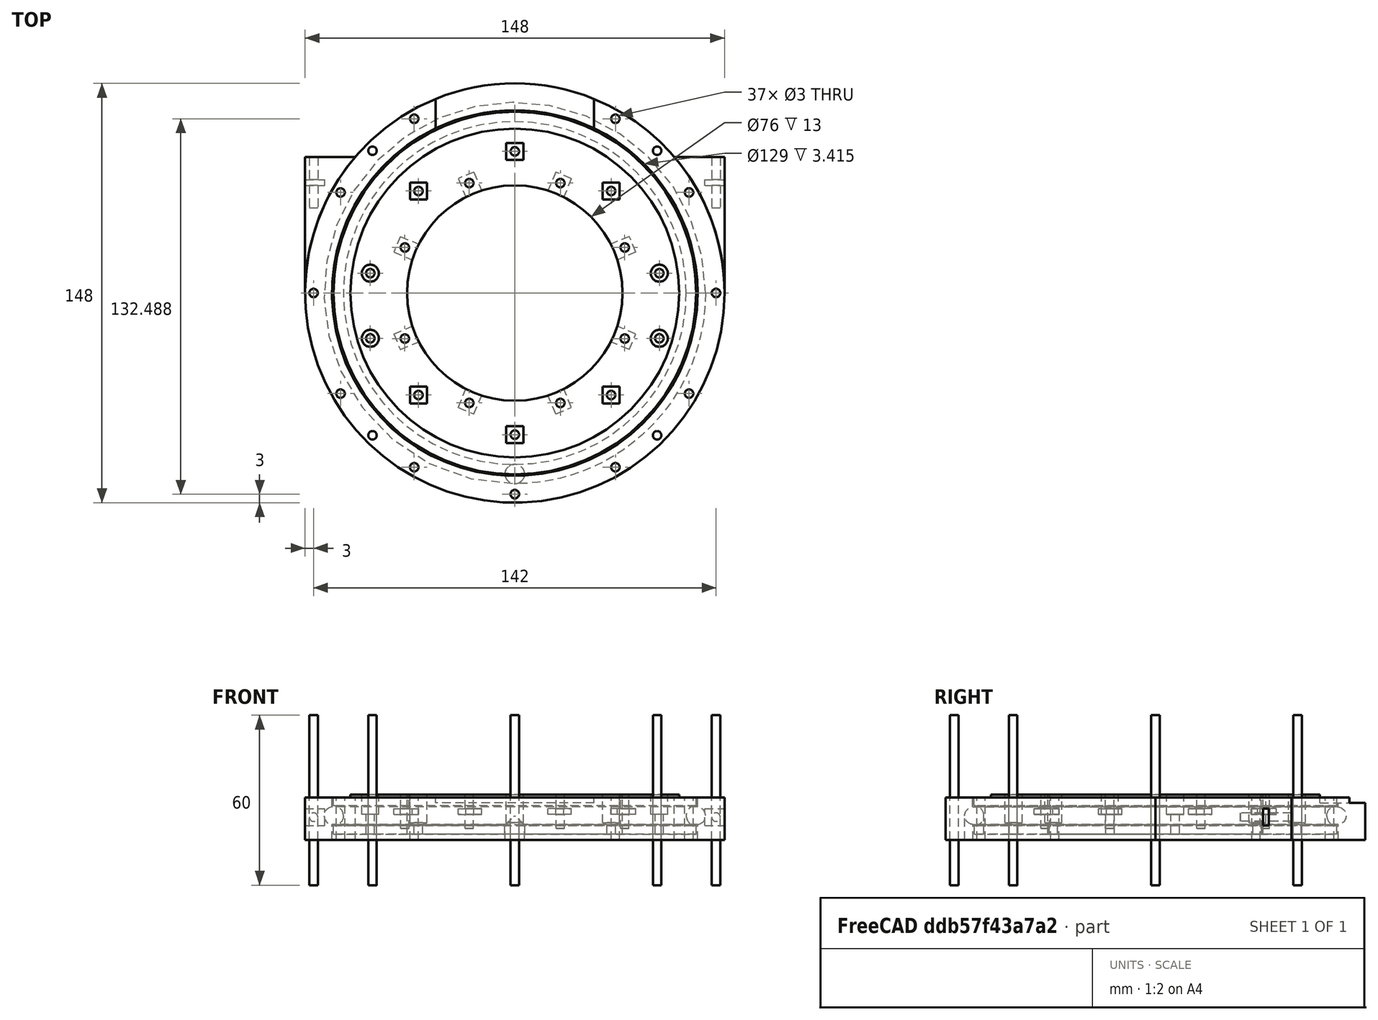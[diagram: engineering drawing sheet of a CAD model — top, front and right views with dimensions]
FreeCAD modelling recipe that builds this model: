
FCSTD DOCUMENT  (FreeCAD 0.19R24291 (Git))
Label: bazovina-part-E_lozo-okruh_011
License: All rights reserved
LicenseURL: http://en.wikipedia.org/wiki/All_rights_reserved
objects: Part::Cylinder×58, Part::Box×24, Part::Cut×18, Part::Compound×14, Part::FeaturePython×3, Part::Torus×2, Mesh::Feature×1
note: 119 computed .brp shape members not serialized (recipe doc carries the construction recipe); baked Part::Feature solids carry a one-line shape summary decoded from their .brp

FEATURE [Part::Torus] Torus001  label="Anuloid001"
  Angle1 = -180
  Angle2 = 180
  Angle3 = 360
  AttacherType = Attacher::AttachEngine3D
  Placement = pos=(0,0,24.5) rot=(0,0,1;0rad)
  Radius1 = 64.2
  Radius2 = 3.1
FEATURE [Part::Cylinder] Cylinder476  label="Válec476"
  Angle = 360
  AttacherType = Attacher::AttachEngine3D
  Height = 20
  Placement = pos=(0,-63.8,4.5) rot=(0,0,1;0rad)
  Radius = 3.5
FEATURE [Part::FeaturePython] Tube024  # WARN: FeaturePython — macro-defined, semantics opaque (R4)
  AttacherType = Attacher::AttachEngine3D
  Height = 15
  InnerRadius = 64.5
  OuterRadius = 74
  Placement = pos=(0,0,16) rot=(0,0,1;0rad)
FEATURE [Part::Cut] Cut
  Base = -> Tube024
  Tool = -> Torus001
FEATURE [Part::Cut] Cut176
  Base = -> Cut
  Tool = -> Cylinder476
FEATURE [Part::Box] Box176  label="Krychle176"
  AttacherType = Attacher::AttachEngine3D
  Height = 15
  Length = 148
  Placement = pos=(-74,0,16) rot=(0,0,1;0rad)
  Width = 48
FEATURE [Part::Cylinder] Cylinder482  label="Válec482"
  Angle = 360
  AttacherType = Attacher::AttachEngine3D
  Height = 15
  Placement = pos=(0,0,16) rot=(0,0,1;0rad)
  Radius = 74
FEATURE [Part::Cut] Cut185
  Base = -> Box176
  Tool = -> Cylinder482
FEATURE [Part::Cylinder] Cylinder485  label="Válec485"
  Angle = 360
  AttacherType = Attacher::AttachEngine3D
  Height = 15
  Placement = pos=(0,0,16) rot=(0,0,1;0rad)
  Radius = 74
FEATURE [Part::Cut] Cut188
  Base = -> Cut185
  Tool = -> Cylinder485
FEATURE [Part::Cylinder] Cylinder510  label="Válec510"
  Angle = 360
  AttacherType = Attacher::AttachEngine3D
  Height = 50
  Placement = pos=(-71,80,24) rot=(1,0,0;1.5708rad)
  Radius = 1.5
FEATURE [Part::Cylinder] Cylinder511  label="Válec511"
  Angle = 360
  AttacherType = Attacher::AttachEngine3D
  Height = 60
  Placement = pos=(0,-71,0) rot=(0,0,1;0rad)
  Radius = 1.5
FEATURE [Part::Cylinder] Cylinder513  label="Válec513"
  Angle = 360
  AttacherType = Attacher::AttachEngine3D
  Height = 60
  Placement = pos=(-50.2046,-50.2046,0) rot=(0,0,-1;0.785398rad)
  Radius = 1.5
FEATURE [Part::Cylinder] Cylinder518  label="Válec518"
  Angle = 360
  AttacherType = Attacher::AttachEngine3D
  Height = 60
  Placement = pos=(71,5e-15,0) rot=(0,0,1;1.5708rad)
  Radius = 1.5
FEATURE [Part::Box] Box209  label="Krychle209"
  AttacherType = Attacher::AttachEngine3D
  Height = 6
  Length = 8
  Placement = pos=(-75,38,21) rot=(0,0,1;0rad)
  Width = 2
FEATURE [Part::Box] Box208  label="Krychle208"
  AttacherType = Attacher::AttachEngine3D
  Height = 6
  Length = 8
  Placement = pos=(67,38,21) rot=(0,0,1;0rad)
  Width = 2
FEATURE [Part::Cylinder] Cylinder517  label="Válec517"
  Angle = 360
  AttacherType = Attacher::AttachEngine3D
  Height = 60
  Placement = pos=(50.2046,50.2046,0) rot=(0,0,1;2.35619rad)
  Radius = 1.5
FEATURE [Part::Cylinder] Cylinder509  label="Válec509"
  Angle = 360
  AttacherType = Attacher::AttachEngine3D
  Height = 50
  Placement = pos=(71,80,24) rot=(1,0,0;1.5708rad)
  Radius = 1.5
FEATURE [Part::Cylinder] Cylinder514  label="Válec514"
  Angle = 360
  AttacherType = Attacher::AttachEngine3D
  Height = 60
  Placement = pos=(-50.2046,50.2046,0) rot=(0,0,1;3.92699rad)
  Radius = 1.5
FEATURE [Part::Cylinder] Cylinder516  label="Válec516"
  Angle = 360
  AttacherType = Attacher::AttachEngine3D
  Height = 60
  Placement = pos=(50.2046,-50.2046,0) rot=(0,0,1;0.785398rad)
  Radius = 1.5
FEATURE [Part::Cylinder] Cylinder512  label="Válec512"
  Angle = 360
  AttacherType = Attacher::AttachEngine3D
  Height = 60
  Placement = pos=(-71,-2.8e-14,0) rot=(0,0,-1;1.5708rad)
  Radius = 1.5
FEATURE [Part::Compound] Compound340
  Links = -> [Cylinder511,Cylinder516,Cylinder518,Cylinder517,Cylinder514,Cylinder512,Cylinder513]
FEATURE [Part::Compound] Compound339
  Links = -> [Cylinder509,Cylinder510]
FEATURE [Part::Compound] Compound338
  Links = -> [Box208,Box209]
FEATURE [Part::Compound] Compound337
  Links = -> [Cut188,Cut176]
FEATURE [Part::Cut] Cut201
  Base = -> Compound337
  Tool = -> Compound338
FEATURE [Part::Cut] Cut202
  Base = -> Cut201
  Tool = -> Compound339
FEATURE [Part::Box] Box179  label="Krychle179"
  AttacherType = Attacher::AttachEngine3D
  Height = 47
  Length = 56
  Placement = pos=(-28,0,29) rot=(0,0,1;0rad)
  Width = 200
FEATURE [Part::Cylinder] Cylinder288  label="Válec288"
  Angle = 360
  AttacherType = Attacher::AttachEngine3D
  Height = 20
  Placement = pos=(0,-64,4.5) rot=(0,0,1;0rad)
  Radius = 3.5
FEATURE [Part::Cylinder] Cylinder372  label="Válec372"
  Angle = 360
  AttacherType = Attacher::AttachEngine3D
  Height = 50
  Placement = pos=(-34,-36,0) rot=(0,0,1;0rad)
  Radius = 1.5
FEATURE [Part::Cylinder] Cylinder371  label="Válec371"
  Angle = 360
  AttacherType = Attacher::AttachEngine3D
  Height = 50
  Placement = pos=(34,36,0) rot=(0,0,1;0rad)
  Radius = 1.5
FEATURE [Part::Torus] Torus  label="Anuloid"
  Angle1 = -180
  Angle2 = 180
  Angle3 = 360
  AttacherType = Attacher::AttachEngine3D
  Placement = pos=(0,0,24.5) rot=(0,0,1;0rad)
  Radius1 = 64
  Radius2 = 3.5
FEATURE [Part::FeaturePython] Tube019  # WARN: FeaturePython — macro-defined, semantics opaque (R4)
  AttacherType = Attacher::AttachEngine3D
  Height = 13
  InnerRadius = 38
  OuterRadius = 64
  Placement = pos=(0,0,18) rot=(0,0,1;0rad)
FEATURE [Part::FeaturePython] Tube020  # WARN: FeaturePython — macro-defined, semantics opaque (R4)
  AttacherType = Attacher::AttachEngine3D
  Height = 1
  InnerRadius = 38
  OuterRadius = 58
  Placement = pos=(0,0,31) rot=(0,0,1;0rad)
FEATURE [Part::Cut] Cut129
  Base = -> Tube019
  Tool = -> Torus
FEATURE [Part::Cut] Cut130
  Base = -> Cut129
  Tool = -> Cylinder288
FEATURE [Part::Cylinder] Cylinder370  label="Válec370"
  Angle = 360
  AttacherType = Attacher::AttachEngine3D
  Height = 50
  Placement = pos=(-34,36,0) rot=(0,0,1;0rad)
  Radius = 1.5
FEATURE [Part::Cylinder] Cylinder374  label="Válec374"
  Angle = 360
  AttacherType = Attacher::AttachEngine3D
  Height = 50
  Placement = pos=(0,50,0) rot=(0,0,1;0rad)
  Radius = 1.5
FEATURE [Part::Cylinder] Cylinder377  label="Válec377"
  Angle = 360
  AttacherType = Attacher::AttachEngine3D
  Height = 50
  Placement = pos=(51,7,0) rot=(0,0,1;0rad)
  Radius = 1.5
FEATURE [Part::Cylinder] Cylinder409  label="Válec409"
  Angle = 360
  AttacherType = Attacher::AttachEngine3D
  Height = 7
  Placement = pos=(51,7,50) rot=(0,0,1;0rad)
  Radius = 3
FEATURE [Part::Cylinder] Cylinder376  label="Válec376"
  Angle = 360
  AttacherType = Attacher::AttachEngine3D
  Height = 100
  Placement = pos=(-51,-16,0) rot=(0,0,1;0rad)
  Radius = 1.5
FEATURE [Part::Cylinder] Cylinder375  label="Válec375"
  Angle = 360
  AttacherType = Attacher::AttachEngine3D
  Height = 50
  Placement = pos=(0,-50,0) rot=(0,0,1;0rad)
  Radius = 1.5
FEATURE [Part::Cylinder] Cylinder404  label="Válec404"
  Angle = 360
  AttacherType = Attacher::AttachEngine3D
  Height = 7
  Placement = pos=(-51,7,50) rot=(0,0,1;0rad)
  Radius = 3
FEATURE [Part::Cylinder] Cylinder373  label="Válec373"
  Angle = 360
  AttacherType = Attacher::AttachEngine3D
  Height = 50
  Placement = pos=(34,-36,0) rot=(0,0,1;0rad)
  Radius = 1.5
FEATURE [Part::Cylinder] Cylinder408  label="Válec408"
  Angle = 360
  AttacherType = Attacher::AttachEngine3D
  Height = 7
  Placement = pos=(-51,-16,50) rot=(0,0,1;0rad)
  Radius = 3
FEATURE [Part::Box] Box149  label="Krychle149"
  AttacherType = Attacher::AttachEngine3D
  Height = 10
  Length = 6
  Placement = pos=(-37,33,40) rot=(0,0,1;0rad)
  Width = 6
FEATURE [Part::Box] Box150  label="Krychle150"
  AttacherType = Attacher::AttachEngine3D
  Height = 10
  Length = 6
  Placement = pos=(31,-39,40) rot=(0,0,1;0rad)
  Width = 6
FEATURE [Part::Cylinder] Cylinder378  label="Válec378"
  Angle = 360
  AttacherType = Attacher::AttachEngine3D
  Height = 50
  Placement = pos=(-51,7,0) rot=(0,0,1;0rad)
  Radius = 1.5
FEATURE [Part::Cylinder] Cylinder379  label="Válec379"
  Angle = 360
  AttacherType = Attacher::AttachEngine3D
  Height = 100
  Placement = pos=(51,-16,0) rot=(0,0,1;0rad)
  Radius = 1.5
FEATURE [Part::Compound] Compound308
  Links = -> [Cylinder370,Cylinder371,Cylinder372,Cylinder373,Cylinder374,Cylinder375,Cylinder376,Cylinder377,Cylinder378,Cylinder379]
FEATURE [Part::Cut] Cut160
  Base = -> Cut130
  Tool = -> Compound308
FEATURE [Part::Cylinder] Cylinder411  label="Válec411"
  Angle = 360
  AttacherType = Attacher::AttachEngine3D
  Height = 7
  Placement = pos=(51,-16,50) rot=(0,0,1;0rad)
  Radius = 3
FEATURE [Part::Cylinder] Cylinder406  label="Válec406"
  Angle = 360
  AttacherType = Attacher::AttachEngine3D
  Height = 7
  Placement = pos=(-51,-16,50) rot=(0,0,1;0rad)
  Radius = 3
FEATURE [Part::Cylinder] Cylinder405  label="Válec405"
  Angle = 360
  AttacherType = Attacher::AttachEngine3D
  Height = 7
  Placement = pos=(51,7,50) rot=(0,0,1;0rad)
  Radius = 3
FEATURE [Part::Box] Box153  label="Krychle153"
  AttacherType = Attacher::AttachEngine3D
  Height = 10
  Length = 6
  Placement = pos=(-37,33,40) rot=(0,0,1;0rad)
  Width = 6
FEATURE [Part::Cylinder] Cylinder410  label="Válec410"
  Angle = 360
  AttacherType = Attacher::AttachEngine3D
  Height = 7
  Placement = pos=(-51,7,50) rot=(0,0,1;0rad)
  Radius = 3
FEATURE [Part::Compound] Compound313
  Links = -> [Cylinder408,Cylinder411,Cylinder409,Cylinder410]
  Placement = pos=(0,0,-25) rot=(0,0,1;0rad)
FEATURE [Part::Cut] Cut162
  Base = -> Cut160
  Tool = -> Compound313
FEATURE [Part::Cylinder] Cylinder407  label="Válec407"
  Angle = 360
  AttacherType = Attacher::AttachEngine3D
  Height = 7
  Placement = pos=(51,-16,50) rot=(0,0,1;0rad)
  Radius = 3
FEATURE [Part::Compound] Compound312
  Links = -> [Cylinder406,Cylinder407,Cylinder405,Cylinder404]
  Placement = pos=(0,0,-25) rot=(0,0,1;0rad)
FEATURE [Part::Cut] Cut161
  Base = -> Tube020
  Tool = -> Compound312
FEATURE [Part::Box] Box148  label="Krychle148"
  AttacherType = Attacher::AttachEngine3D
  Height = 10
  Length = 6
  Placement = pos=(31,33,40) rot=(0,0,1;0rad)
  Width = 6
FEATURE [Part::Box] Box146  label="Krychle146"
  AttacherType = Attacher::AttachEngine3D
  Height = 10
  Length = 6
  Placement = pos=(-3,-53,40) rot=(0,0,1;0rad)
  Width = 6
FEATURE [Part::Box] Box145  label="Krychle145"
  AttacherType = Attacher::AttachEngine3D
  Height = 10
  Length = 6
  Placement = pos=(-3,47,40) rot=(0,0,1;0rad)
  Width = 6
FEATURE [Part::Box] Box147  label="Krychle147"
  AttacherType = Attacher::AttachEngine3D
  Height = 10
  Length = 6
  Placement = pos=(-37,-39,40) rot=(0,0,1;0rad)
  Width = 6
FEATURE [Part::Compound] Compound315
  Links = -> [Box145,Box147,Box146,Box148,Box149,Box150]
  Placement = pos=(0,0,-18) rot=(0,0,1;0rad)
FEATURE [Part::Cut] Cut164
  Base = -> Cut162
  Tool = -> Compound315
FEATURE [Part::Box] Box151  label="Krychle151"
  AttacherType = Attacher::AttachEngine3D
  Height = 10
  Length = 6
  Placement = pos=(-3,-53,40) rot=(0,0,1;0rad)
  Width = 6
FEATURE [Part::Box] Box157  label="Krychle157"
  AttacherType = Attacher::AttachEngine3D
  Height = 2
  Length = 6
  Placement = pos=(14.4491,-42.7226,25) rot=(0,0,1;0.392699rad)
  Width = 8
FEATURE [Part::Box] Box162  label="Krychle162"
  AttacherType = Attacher::AttachEngine3D
  Height = 2
  Length = 6
  Placement = pos=(-40.4265,19.9924,25) rot=(0,0,-1;1.96349rad)
  Width = 8
FEATURE [Part::Box] Box159  label="Krychle159"
  AttacherType = Attacher::AttachEngine3D
  Height = 2
  Length = 6
  Placement = pos=(42.7226,14.4491,25) rot=(0,0,1;1.96349rad)
  Width = 8
FEATURE [Part::Box] Box156  label="Krychle156"
  AttacherType = Attacher::AttachEngine3D
  Height = 10
  Length = 6
  Placement = pos=(31,-39,40) rot=(0,0,1;0rad)
  Width = 6
FEATURE [Part::Box] Box154  label="Krychle154"
  AttacherType = Attacher::AttachEngine3D
  Height = 10
  Length = 6
  Placement = pos=(-37,-39,40) rot=(0,0,1;0rad)
  Width = 6
FEATURE [Part::Box] Box158  label="Krychle158"
  AttacherType = Attacher::AttachEngine3D
  Height = 2
  Length = 6
  Placement = pos=(40.4265,-19.9924,25) rot=(0,0,1;1.1781rad)
  Width = 8
FEATURE [Part::Box] Box152  label="Krychle152"
  AttacherType = Attacher::AttachEngine3D
  Height = 10
  Length = 6
  Placement = pos=(-3,47,40) rot=(0,0,1;0rad)
  Width = 6
FEATURE [Part::Box] Box155  label="Krychle155"
  AttacherType = Attacher::AttachEngine3D
  Height = 10
  Length = 6
  Placement = pos=(31,33,40) rot=(0,0,1;0rad)
  Width = 6
FEATURE [Part::Compound] Compound316
  Links = -> [Box152,Box154,Box151,Box155,Box153,Box156]
  Placement = pos=(0,0,-18) rot=(0,0,1;0rad)
FEATURE [Part::Cut] Cut163
  Base = -> Cut161
  Tool = -> Compound316
FEATURE [Part::Cylinder] Cylinder471  label="Válec471"
  Angle = 360
  AttacherType = Attacher::AttachEngine3D
  Height = 100
  Placement = pos=(16.0727,38.8029,0) rot=(0,0,1;3.14159rad)
  Radius = 1.5
FEATURE [Part::Cylinder] Cylinder474  label="Válec474"
  Angle = 360
  AttacherType = Attacher::AttachEngine3D
  Height = 100
  Placement = pos=(-38.8029,-16.0727,0) rot=(0,0,-1;0.785398rad)
  Radius = 1.5
FEATURE [Part::Box] Box163  label="Krychle163"
  AttacherType = Attacher::AttachEngine3D
  Height = 2
  Length = 6
  Placement = pos=(-42.7226,-14.4491,25) rot=(0,0,-1;1.1781rad)
  Width = 8
FEATURE [Part::Cylinder] Cylinder446  label="Válec446"
  Angle = 360
  AttacherType = Attacher::AttachEngine3D
  Height = 100
  Placement = pos=(38.8029,16.0727,0) rot=(0,0,1;2.35619rad)
  Radius = 1.5
FEATURE [Part::Cylinder] Cylinder448  label="Válec448"
  Angle = 360
  AttacherType = Attacher::AttachEngine3D
  Height = 100
  Placement = pos=(-16.0727,38.8029,0) rot=(0,0,1;3.92699rad)
  Radius = 1.5
FEATURE [Part::Box] Box161  label="Krychle161"
  AttacherType = Attacher::AttachEngine3D
  Height = 2
  Length = 6
  Placement = pos=(-14.4491,42.7226,25) rot=(0,0,1;3.53429rad)
  Width = 8
FEATURE [Part::Cylinder] Cylinder449  label="Válec449"
  Angle = 360
  AttacherType = Attacher::AttachEngine3D
  Height = 100
  Placement = pos=(-38.8029,16.0727,0) rot=(0,0,-1;1.5708rad)
  Radius = 1.5
FEATURE [Part::Cylinder] Cylinder451  label="Válec451"
  Angle = 360
  AttacherType = Attacher::AttachEngine3D
  Height = 100
  Placement = pos=(-16.0727,-38.8029,0) rot=(0,0,1;0rad)
  Radius = 1.5
FEATURE [Part::Cylinder] Cylinder444  label="Válec444"
  Angle = 360
  AttacherType = Attacher::AttachEngine3D
  Height = 100
  Placement = pos=(16.0727,-38.8029,0) rot=(0,0,1;0.785398rad)
  Radius = 1.5
FEATURE [Part::Cylinder] Cylinder473  label="Válec473"
  Angle = 360
  AttacherType = Attacher::AttachEngine3D
  Height = 100
  Placement = pos=(-38.8029,16.0727,0) rot=(0,0,-1;1.5708rad)
  Radius = 1.5
FEATURE [Part::Box] Box164  label="Krychle164"
  AttacherType = Attacher::AttachEngine3D
  Height = 2
  Length = 6
  Placement = pos=(-19.9924,-40.4265,25) rot=(0,0,-1;0.392699rad)
  Width = 8
FEATURE [Part::Box] Box160  label="Krychle160"
  AttacherType = Attacher::AttachEngine3D
  Height = 2
  Length = 6
  Placement = pos=(19.9924,40.4265,25) rot=(0,0,1;2.74889rad)
  Width = 8
FEATURE [Part::Compound] Compound322
  Links = -> [Box157,Box158,Box159,Box160,Box161,Box162,Box163,Box164]
FEATURE [Part::Cylinder] Cylinder445  label="Válec445"
  Angle = 360
  AttacherType = Attacher::AttachEngine3D
  Height = 100
  Placement = pos=(38.8029,-16.0727,0) rot=(0,0,1;1.5708rad)
  Radius = 1.5
FEATURE [Part::Cylinder] Cylinder450  label="Válec450"
  Angle = 360
  AttacherType = Attacher::AttachEngine3D
  Height = 100
  Placement = pos=(-38.8029,-16.0727,0) rot=(0,0,-1;0.785398rad)
  Radius = 1.5
FEATURE [Part::Cylinder] Cylinder447  label="Válec447"
  Angle = 360
  AttacherType = Attacher::AttachEngine3D
  Height = 100
  Placement = pos=(16.0727,38.8029,0) rot=(0,0,1;3.14159rad)
  Radius = 1.5
FEATURE [Part::Compound] Compound325
  Links = -> [Cylinder444,Cylinder445,Cylinder446,Cylinder447,Cylinder448,Cylinder449,Cylinder450,Cylinder451]
FEATURE [Part::Cut] Cut173
  Base = -> Cut163
  Tool = -> Compound325
FEATURE [Part::Cylinder] Cylinder468  label="Válec468"
  Angle = 360
  AttacherType = Attacher::AttachEngine3D
  Height = 100
  Placement = pos=(16.0727,-38.8029,0) rot=(0,0,1;0.785398rad)
  Radius = 1.5
FEATURE [Part::Cylinder] Cylinder469  label="Válec469"
  Angle = 360
  AttacherType = Attacher::AttachEngine3D
  Height = 100
  Placement = pos=(38.8029,-16.0727,0) rot=(0,0,1;1.5708rad)
  Radius = 1.5
FEATURE [Part::Cylinder] Cylinder472  label="Válec472"
  Angle = 360
  AttacherType = Attacher::AttachEngine3D
  Height = 100
  Placement = pos=(-16.0727,38.8029,0) rot=(0,0,1;3.92699rad)
  Radius = 1.5
FEATURE [Part::Cylinder] Cylinder470  label="Válec470"
  Angle = 360
  AttacherType = Attacher::AttachEngine3D
  Height = 100
  Placement = pos=(38.8029,16.0727,0) rot=(0,0,1;2.35619rad)
  Radius = 1.5
FEATURE [Part::Cylinder] Cylinder475  label="Válec475"
  Angle = 360
  AttacherType = Attacher::AttachEngine3D
  Height = 100
  Placement = pos=(-16.0727,-38.8029,0) rot=(0,0,1;0rad)
  Radius = 1.5
FEATURE [Part::Compound] Compound328
  Links = -> [Cylinder468,Cylinder469,Cylinder470,Cylinder471,Cylinder472,Cylinder473,Cylinder474,Cylinder475]
  Placement = pos=(0,0,20) rot=(0,0,1;0rad)
FEATURE [Part::Cut] Cut174
  Base = -> Cut164
  Tool = -> Compound328
FEATURE [Part::Cut] Cut175
  Base = -> Cut174
  Tool = -> Compound322
FEATURE [Part::Compound] Compound336  label="bazovina-part-C"
  Links = -> [Cut173,Cut175]
FEATURE [Part::Cylinder] Cylinder974  label="Válec974"
  Angle = 360
  AttacherType = Attacher::AttachEngine3D
  Height = 60
  Placement = pos=(35.5,-61.4878,0) rot=(0,0,1;0.523599rad)
  Radius = 1.5
FEATURE [Part::Cylinder] Cylinder976  label="Válec976"
  Angle = 360
  AttacherType = Attacher::AttachEngine3D
  Height = 60
  Placement = pos=(71,-1.8e-14,0) rot=(0,0,1;1.5708rad)
  Radius = 1.5
FEATURE [Part::Cylinder] Cylinder973  label="Válec973"
  Angle = 360
  AttacherType = Attacher::AttachEngine3D
  Height = 60
  Placement = pos=(0,-71,0) rot=(0,0,1;0rad)
  Radius = 1.5
FEATURE [Part::Cylinder] Cylinder975  label="Válec975"
  Angle = 360
  AttacherType = Attacher::AttachEngine3D
  Height = 60
  Placement = pos=(61.4878,-35.5,0) rot=(0,0,1;1.0472rad)
  Radius = 1.5
FEATURE [Part::Cylinder] Cylinder978  label="Válec978"
  Angle = 360
  AttacherType = Attacher::AttachEngine3D
  Height = 60
  Placement = pos=(35.5,61.4878,0) rot=(0,0,1;2.61799rad)
  Radius = 1.5
FEATURE [Part::Cylinder] Cylinder981  label="Válec981"
  Angle = 360
  AttacherType = Attacher::AttachEngine3D
  Height = 60
  Placement = pos=(-61.4878,35.5,0) rot=(0,0,1;4.18879rad)
  Radius = 1.5
FEATURE [Part::Cylinder] Cylinder982  label="Válec982"
  Angle = 360
  AttacherType = Attacher::AttachEngine3D
  Height = 60
  Placement = pos=(-71,2.7e-14,0) rot=(0,0,-1;1.5708rad)
  Radius = 1.5
FEATURE [Part::Cylinder] Cylinder983  label="Válec983"
  Angle = 360
  AttacherType = Attacher::AttachEngine3D
  Height = 60
  Placement = pos=(-61.4878,-35.5,0) rot=(0,0,-1;1.0472rad)
  Radius = 1.5
FEATURE [Part::Cylinder] Cylinder980  label="Válec980"
  Angle = 360
  AttacherType = Attacher::AttachEngine3D
  Height = 60
  Placement = pos=(-35.5,61.4878,0) rot=(0,0,1;3.66519rad)
  Radius = 1.5
FEATURE [Part::Cylinder] Cylinder977  label="Válec977"
  Angle = 360
  AttacherType = Attacher::AttachEngine3D
  Height = 60
  Placement = pos=(61.4878,35.5,0) rot=(0,0,1;2.0944rad)
  Radius = 1.5
FEATURE [Part::Cylinder] Cylinder984  label="Válec984"
  Angle = 360
  AttacherType = Attacher::AttachEngine3D
  Height = 60
  Placement = pos=(-35.5,-61.4878,0) rot=(0,0,-1;0.523599rad)
  Radius = 1.5
FEATURE [Part::Compound] Compound525
  Links = -> [Cylinder973,Cylinder974,Cylinder975,Cylinder976,Cylinder977,Cylinder978,Cylinder980,Cylinder981,Cylinder982,Cylinder983,Cylinder984]
FEATURE [Part::Cut] Cut203
  Base = -> Cut202
  Tool = -> Box179
FEATURE [Part::Cut] Cut204  label="bazovina_part-E_lozo-okruh-novo"
  Base = -> Cut203
  Tool = -> Compound525
FEATURE [Mesh::Feature] Mesh  label="bazovina_part-E_lozo-okruh-novo (Meshed)"
